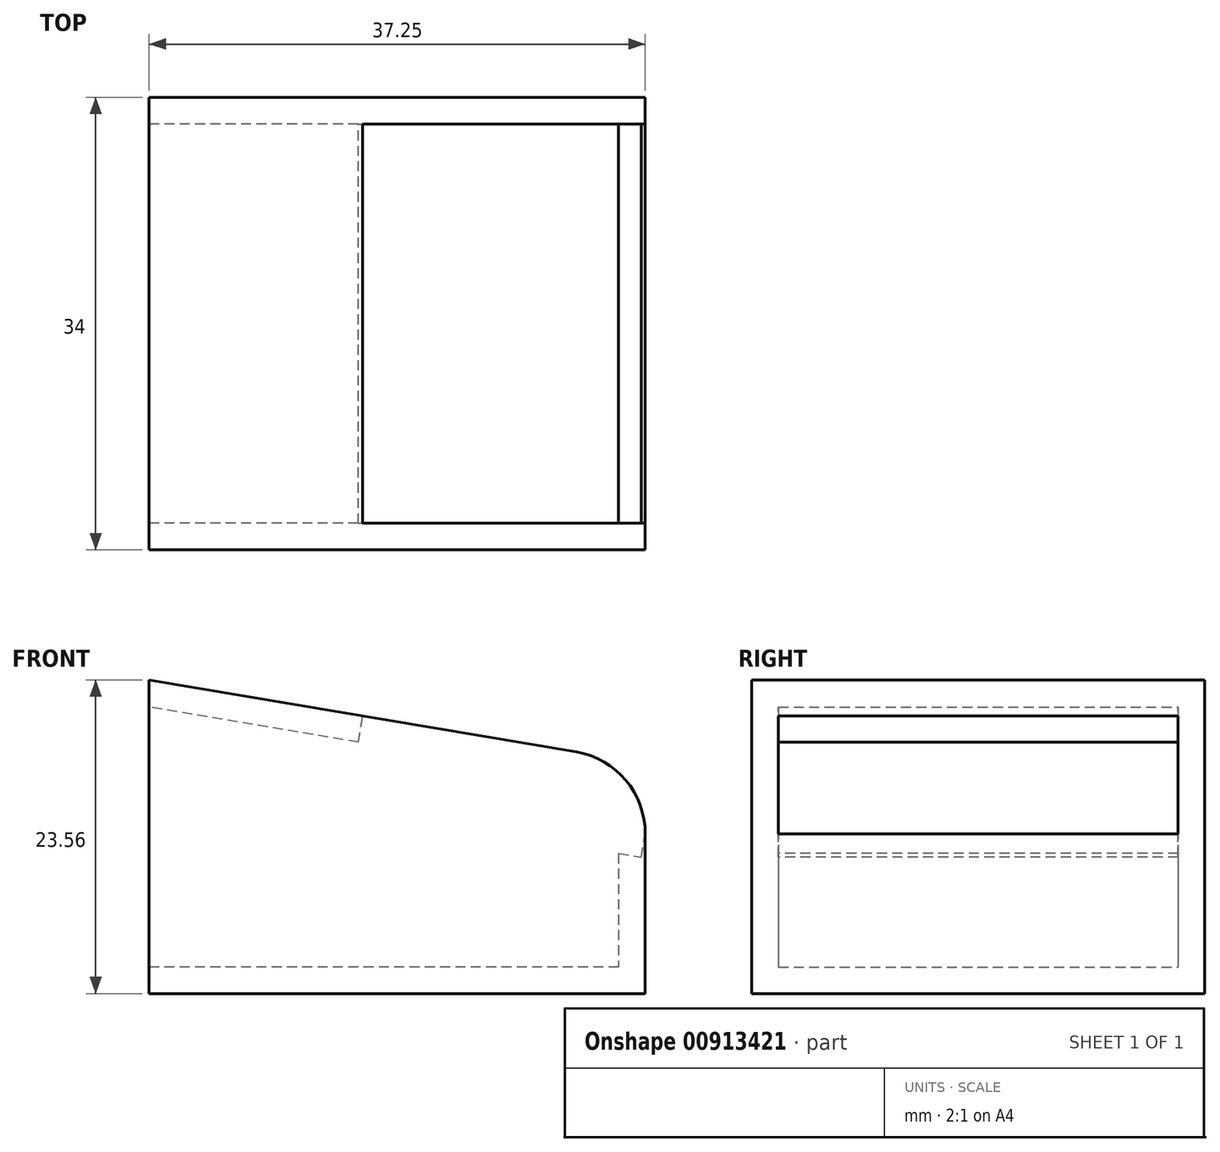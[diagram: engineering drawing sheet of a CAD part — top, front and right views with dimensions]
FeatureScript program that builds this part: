
annotation { "Feature Type Name" : "Feature", "Feature Type Description" : "" }
export const myFeature = defineFeature(function(context is Context, id is Id, definition is map)
    precondition{}
    {
        {
            var Q0;
            Q0=qCreatedBy(makeId("Front.planeOp"),FACE);
            var sketch = newSketch(context, id + "F0", { "sketchPlane" : qUnion([Q0])});
            skPoint(sketch, "E0.middle", {"position": v(0, 0) * mm});
            skCircle(sketch, "E1", {"center": v(20, 10) * mm, "radius": 2.5 * mm});
            skLineSegment(sketch, "E2", {"start": v(20, 10) * mm, "end": v(20.43, 12.46) * mm});
            skLineSegment(sketch, "E3", {"start": v(20.43, 12.46) * mm, "end": v(19.57, 7.54) * mm});
            skLineSegment(sketch, "E4", {"start": v(19.57, 7.54) * mm, "end": v(-29.67, 16.22) * mm});
            skLineSegment(sketch, "E5", {"start": v(-29.24, 18.68) * mm, "end": v(-20.87, 17.2) * mm});
            skLineSegment(sketch, "E6", {"start": v(-20.87, 17.2) * mm, "end": v(-20.44, 19.67) * mm});
            skLineSegment(sketch, "E7", {"start": v(-20.44, 19.67) * mm, "end": v(20.43, 12.46) * mm});
            skLineSegment(sketch, "E8", {"start": v(-29.24, 18.68) * mm, "end": v(-29.67, 16.22) * mm});
            skSolve(sketch);
        }
        {
            var Q0;
            Q0=qCreatedBy(makeId("Front.planeOp"),FACE);
            var sketch = newSketch(context, id + "F1", { "sketchPlane" : qUnion([Q0])});
            skPoint(sketch, "E9", {"position": v(20, 10) * mm});
            skPoint(sketch, "E10", {"position": v(-11, 19.53) * mm});
            skLineSegment(sketch, "E11", {"start": v(-11, 19.53) * mm, "end": v(-11, 0) * mm});
            skLineSegment(sketch, "E12", {"start": v(24.25, 10) * mm, "end": v(24.25, 0) * mm});
            skLineSegment(sketch, "E13", {"start": v(24.25, 0) * mm, "end": v(-11, 0) * mm});
            skLineSegment(sketch, "E14", {"start": v(20.74, 14.19) * mm, "end": v(-11, 19.53) * mm});
            skArc(sketch, "E15", {"start": v(20.74, 14.19) * mm, "mid": v(23.26, 12.73) * mm, "end": v(24.25, 10) * mm});
            skSolve(sketch);
        }
        {
            var Q0;
            Q0=makeQuery(id+"F1.imprint","IMPRINT",FACE,{"disambiguationData":[TD([[makeQuery(id+"F1.imprint","IMPRINT",EDGE,{"derivedFrom":sQuery(id+"F1.wireOp",EDGE,"E11")}),1.0]])]});
            extrude(context, id + "F2", {"entities" : qUnion([Q0]), "endBound" : BoundingType.SYMMETRIC, "depth" : 30 * mm, "offsetDistance" : 25 * mm});
        }
        {
            var Q0;
            Q0=makeQuery(id+"F2.opExtrude","SWEPT_FACE",FACE,{"disambiguationData":[OSD([sQuery(id+"F1.wireOp",EDGE,"E11")])]});
            shell(context, id + "F3", {"entities" : qUnion([Q0]), "thickness" : 2 * mm, "oppositeDirection" : true});
        }
        {
            var Q0;
            Q0=makeQuery(id+"F2.opExtrude","SWEPT_FACE",FACE,{"disambiguationData":[OSD([sQuery(id+"F1.wireOp",EDGE,"E14")])]});
            cPlane(context, id + "F4", {"entities" : qUnion([Q0]), "cplaneType" : CPlaneType.OFFSET, "offset" : 0 * mm, "width" : 150 * mm, "height" : 150 * mm});
        }
        {
            var Q0;
            Q0=qCreatedBy(id+"F4.planeOp",FACE);
            var sketch = newSketch(context, id + "F5", { "sketchPlane" : qUnion([Q0])});
            skPoint(sketch, "E16", {"position": v(-14.43, 17) * mm});
            skPoint(sketch, "E17", {"position": v(18.1, 17) * mm});
            skPoint(sketch, "E18", {"position": v(18.1, -17) * mm});
            skPoint(sketch, "E19", {"position": v(-14.43, -17) * mm});
            skLineSegment(sketch, "E20", {"start": v(-14.43, 17) * mm, "end": v(18.1, 17) * mm});
            skLineSegment(sketch, "E21", {"start": v(18.1, -17) * mm, "end": v(-14.43, -17) * mm});
            skLineSegment(sketch, "E22", {"start": v(-14.43, 17) * mm, "end": v(-14.43, -17) * mm});
            skLineSegment(sketch, "E23", {"start": v(1.84, 15) * mm, "end": v(1.84, -15) * mm});
            skPoint(sketch, "E24", {"position": v(24.23, -17) * mm});
            skPoint(sketch, "E25", {"position": v(24.23, 17) * mm});
            skLineSegment(sketch, "E26", {"start": v(24.23, 15) * mm, "end": v(24.23, -15) * mm});
            skLineSegment(sketch, "E27", {"start": v(1.84, 15) * mm, "end": v(24.23, 15) * mm});
            skLineSegment(sketch, "E28", {"start": v(1.84, -15) * mm, "end": v(24.23, -15) * mm});
            skSolve(sketch);
        }
        {
            var Q0;
            Q0=makeQuery(id+"F5.imprint","IMPRINT",FACE,{"disambiguationData":[TD([[makeQuery(id+"F5.imprint","IMPRINT",EDGE,{"derivedFrom":sQuery(id+"F5.wireOp",EDGE,"E23")}),1.0]])]});
            extrude(context, id + "F6", {"entities" : qUnion([Q0]), "operationType" : NewBodyOperationType.REMOVE, "oppositeDirection" : true, "depth" : 7 * mm, "offsetDistance" : 25 * mm});
        }
    });
